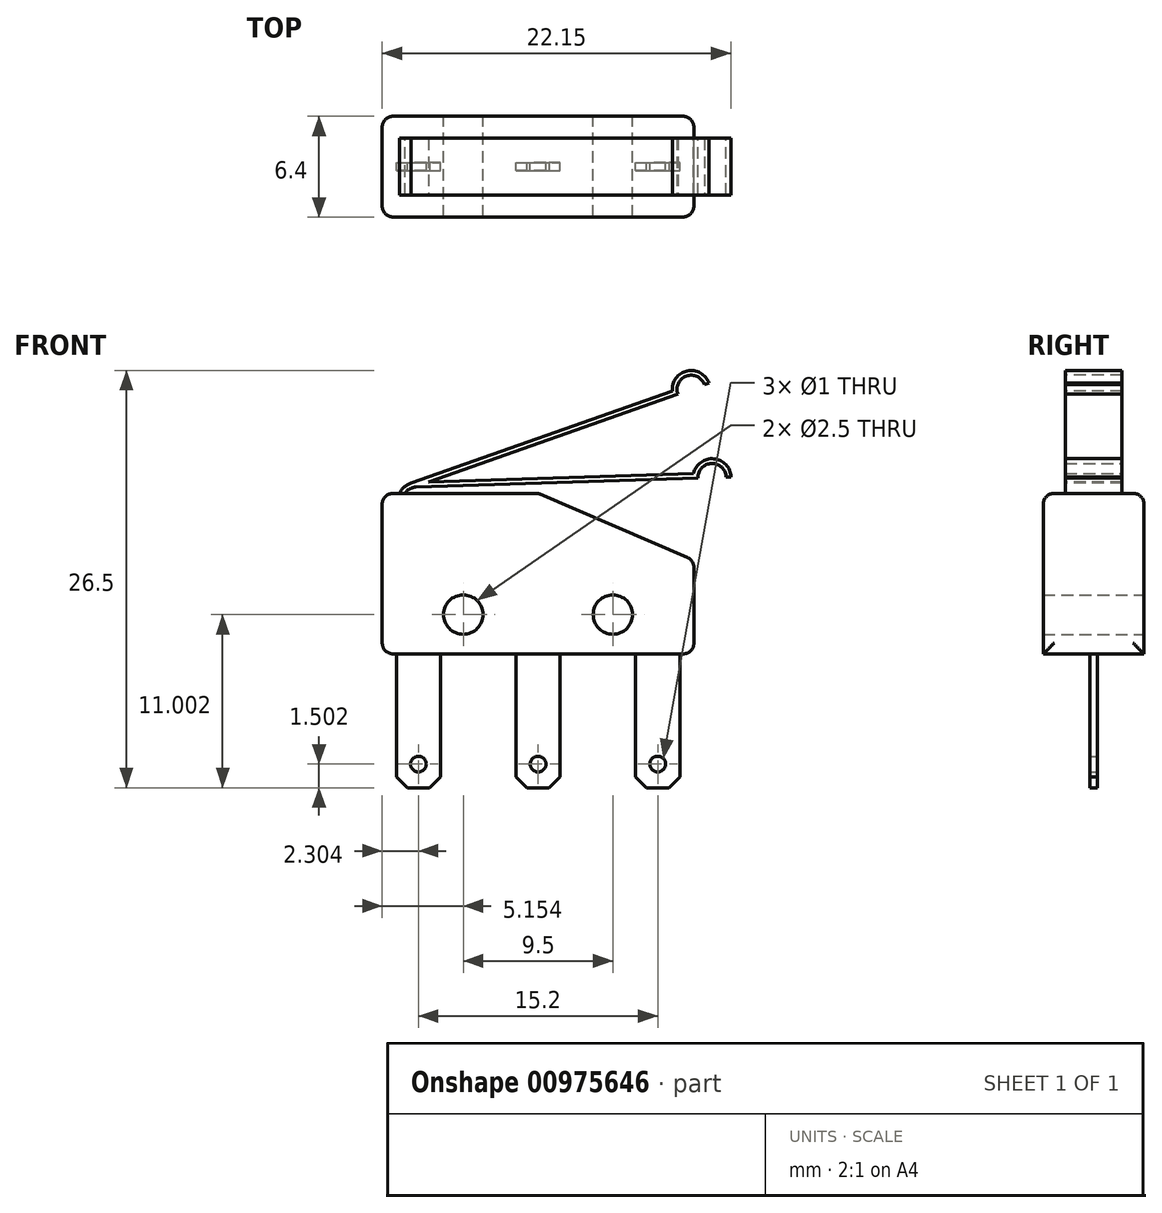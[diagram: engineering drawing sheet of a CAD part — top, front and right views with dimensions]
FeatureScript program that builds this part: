
annotation { "Feature Type Name" : "Feature", "Feature Type Description" : "" }
export const myFeature = defineFeature(function(context is Context, id is Id, definition is map)
    precondition{}
    {
        {
            var Q0;
            Q0=qCreatedBy(makeId("Front.planeOp"),FACE);
            var sketch = newSketch(context, id + "F0", { "sketchPlane" : qUnion([Q0])});
            skLineSegment(sketch, "E0.bottom", {"start": v(-24.17, 13.96) * mm, "end": v(-14.27, 13.96) * mm});
            skLineSegment(sketch, "E0.top", {"start": v(-24.17, 3.76) * mm, "end": v(-4.37, 3.76) * mm});
            skLineSegment(sketch, "E0.left", {"start": v(-24.17, 13.96) * mm, "end": v(-24.17, 3.76) * mm});
            skLineSegment(sketch, "E0.right", {"start": v(-4.37, 9.71) * mm, "end": v(-4.37, 3.76) * mm});
            skLineSegment(sketch, "E1", {"start": v(-24.17, 6.26) * mm, "end": v(-4.37, 6.26) * mm, "construction": true});
            skLineSegment(sketch, "E2", {"start": v(-14.27, 13.96) * mm, "end": v(-4.37, 9.71) * mm});
            skCircle(sketch, "E3", {"center": v(-19.02, 6.26) * mm, "radius": 1.25 * mm});
            skCircle(sketch, "E4", {"center": v(-9.52, 6.26) * mm, "radius": 1.25 * mm});
            skSolve(sketch);
        }
        {
            var Q0;
            Q0 = qSketchRegion(id + "F0", true);
            extrude(context, id + "F1", {"entities" : qUnion([Q0]), "endBound" : BoundingType.SYMMETRIC, "depth" : 6.4 * mm, "offsetDistance" : 25 * mm});
        }
        {
            var Q0;
            Q0=makeQuery(id+"F1.opExtrude","SWEPT_EDGE",EDGE,{"disambiguationData":[OSD([sQuery(id+"F0.wireOp",EDGE,"E0.right"),sQuery(id+"F0.wireOp",EDGE,"E2")])]});
            var Q1;
            Q1=makeQuery(id+"F1.opExtrude","SWEPT_EDGE",EDGE,{"disambiguationData":[OSD([sQuery(id+"F0.wireOp",EDGE,"E0.bottom"),sQuery(id+"F0.wireOp",EDGE,"E2")])]});
            var Q2;
            Q2=makeQuery(id+"F1.opExtrude","SWEPT_EDGE",EDGE,{"disambiguationData":[OSD([sQuery(id+"F0.wireOp",EDGE,"E0.bottom"),sQuery(id+"F0.wireOp",EDGE,"E0.left")])]});
            var Q3;
            Q3=makeQuery(id+"F1.opExtrude","SWEPT_EDGE",EDGE,{"disambiguationData":[OSD([sQuery(id+"F0.wireOp",EDGE,"E0.top"),sQuery(id+"F0.wireOp",EDGE,"E0.right")])]});
            var Q4;
            Q4=makeQuery(id+"F1.opExtrude","SWEPT_EDGE",EDGE,{"disambiguationData":[OSD([sQuery(id+"F0.wireOp",EDGE,"E0.top"),sQuery(id+"F0.wireOp",EDGE,"E0.left")])]});
            var Q5;
            Q5=makeQuery(id+"F1.opExtrude","CAP_EDGE",EDGE,{"disambiguationData":[OSD([sQuery(id+"F0.wireOp",EDGE,"E0.bottom")])],"isStart":false});
            var Q6;
            Q6=makeQuery(id+"F1.opExtrude","CAP_EDGE",EDGE,{"disambiguationData":[OSD([sQuery(id+"F0.wireOp",EDGE,"E2")])],"isStart":false});
            var Q7;
            Q7=makeQuery(id+"F1.opExtrude","CAP_EDGE",EDGE,{"disambiguationData":[OSD([sQuery(id+"F0.wireOp",EDGE,"E0.right")])],"isStart":false});
            var Q8;
            Q8=makeQuery(id+"F1.opExtrude","CAP_EDGE",EDGE,{"disambiguationData":[OSD([sQuery(id+"F0.wireOp",EDGE,"E0.right")])],"isStart":true});
            var Q9;
            Q9=makeQuery(id+"F1.opExtrude","CAP_EDGE",EDGE,{"disambiguationData":[OSD([sQuery(id+"F0.wireOp",EDGE,"E2")])],"isStart":true});
            var Q10;
            Q10=makeQuery(id+"F1.opExtrude","CAP_EDGE",EDGE,{"disambiguationData":[OSD([sQuery(id+"F0.wireOp",EDGE,"E0.bottom")])],"isStart":true});
            var Q11;
            Q11=makeQuery(id+"F1.opExtrude","CAP_EDGE",EDGE,{"disambiguationData":[OSD([sQuery(id+"F0.wireOp",EDGE,"E0.left")])],"isStart":false});
            var Q12;
            Q12=makeQuery(id+"F1.opExtrude","CAP_EDGE",EDGE,{"disambiguationData":[OSD([sQuery(id+"F0.wireOp",EDGE,"E0.left")])],"isStart":true});
            fillet(context, id + "F2", {"entities" : qUnion([Q0, Q1, Q2, Q3, Q4, Q5, Q6, Q7, Q8, Q9, Q10, Q11, Q12]), "tangentPropagation" : true, "radius" : 0.7 * mm, "defaultsChanged" : true, "vertexSettings" : [], "allowEdgeOverflow" : false});
        }
        {
            var Q0;
            Q0=qCreatedBy(makeId("Front.planeOp"),FACE);
            var sketch = newSketch(context, id + "F3", { "sketchPlane" : qUnion([Q0])});
            skLineSegment(sketch, "E5", {"start": v(-22.02, 14.66) * mm, "end": v(-4.39, 15.23) * mm});
            skLineSegment(sketch, "E6", {"start": v(-2.02, 15) * mm, "end": v(-2.32, 15) * mm});
            skLineSegment(sketch, "E7", {"start": v(-22, 14.36) * mm, "end": v(-22.02, 14.66) * mm, "construction": true});
            skArc(sketch, "E8", {"start": v(-2.32, 15) * mm, "mid": v(-3.24, 15.86) * mm, "end": v(-4.12, 14.93) * mm});
            skArc(sketch, "E9", {"start": v(-2.02, 15) * mm, "mid": v(-3.1, 16.16) * mm, "end": v(-4.39, 15.23) * mm});
            skLineSegment(sketch, "E10.trimOffspring", {"start": v(-4.12, 14.93) * mm, "end": v(-22, 14.36) * mm});
            skLineSegment(sketch, "E11", {"start": v(-23.44, 16.16) * mm, "end": v(-4.46, 16.16) * mm, "construction": true});
            skLineSegment(sketch, "E12", {"start": v(-19.02, 16.68) * mm, "end": v(-19.02, 5.07) * mm, "construction": true});
            skArc(sketch, "E13", {"start": v(-22.02, 14.66) * mm, "mid": v(-23.17, 13.57) * mm, "end": v(-22.22, 12.3) * mm});
            skArc(sketch, "E14", {"start": v(-22, 14.36) * mm, "mid": v(-22.86, 13.58) * mm, "end": v(-22.22, 12.61) * mm});
            skLineSegment(sketch, "E15", {"start": v(-22.22, 12.61) * mm, "end": v(-22.22, 12.3) * mm});
            skLineSegment(sketch, "E16", {"start": v(-23.32, 21.76) * mm, "end": v(-4.44, 21.76) * mm, "construction": true});
            skLineSegment(sketch, "E17", {"start": v(-3.22, 14.96) * mm, "end": v(-3.22, 23.39) * mm, "construction": true});
            skSolve(sketch);
        }
        {
            var Q0;
            Q0 = qSketchRegion(id + "F3", true);
            extrude(context, id + "F4", {"entities" : qUnion([Q0]), "operationType" : NewBodyOperationType.ADD, "endBound" : BoundingType.SYMMETRIC, "depth" : 3.6 * mm, "offsetDistance" : 25 * mm});
        }
        {
            var Q0;
            Q0=qCreatedBy(makeId("Front.planeOp"),FACE);
            var sketch = newSketch(context, id + "F5", { "sketchPlane" : qUnion([Q0])});
            skLineSegment(sketch, "E18.bottom", {"start": v(-23.27, 4.32) * mm, "end": v(-20.47, 4.32) * mm});
            skLineSegment(sketch, "E18.top", {"start": v(-23.27, -4.74) * mm, "end": v(-20.47, -4.74) * mm});
            skLineSegment(sketch, "E18.left", {"start": v(-23.27, 4.32) * mm, "end": v(-23.27, -4.74) * mm});
            skLineSegment(sketch, "E18.right", {"start": v(-20.47, 4.32) * mm, "end": v(-20.47, -4.74) * mm});
            skLineSegment(sketch, "E19.bottom", {"start": v(-15.67, 4.32) * mm, "end": v(-12.87, 4.32) * mm});
            skLineSegment(sketch, "E19.top", {"start": v(-15.67, -4.74) * mm, "end": v(-12.87, -4.74) * mm});
            skLineSegment(sketch, "E19.left", {"start": v(-15.67, 4.32) * mm, "end": v(-15.67, -4.74) * mm});
            skLineSegment(sketch, "E19.right", {"start": v(-12.87, 4.32) * mm, "end": v(-12.87, -4.74) * mm});
            skLineSegment(sketch, "E20.bottom", {"start": v(-8.07, 4.32) * mm, "end": v(-5.27, 4.32) * mm});
            skLineSegment(sketch, "E20.top", {"start": v(-8.07, -4.74) * mm, "end": v(-5.27, -4.74) * mm});
            skLineSegment(sketch, "E20.left", {"start": v(-8.07, 4.32) * mm, "end": v(-8.07, -4.74) * mm});
            skLineSegment(sketch, "E20.right", {"start": v(-5.27, 4.32) * mm, "end": v(-5.27, -4.74) * mm});
            skLineSegment(sketch, "E21", {"start": v(-21.87, -4.74) * mm, "end": v(-21.87, 4.32) * mm, "construction": true});
            skLineSegment(sketch, "E22", {"start": v(-21.87, 4.32) * mm, "end": v(-14.27, -4.74) * mm, "construction": true});
            skLineSegment(sketch, "E23", {"start": v(-14.27, -4.74) * mm, "end": v(-14.27, 4.32) * mm, "construction": true});
            skLineSegment(sketch, "E24", {"start": v(-14.27, 4.32) * mm, "end": v(-6.67, -4.74) * mm, "construction": true});
            skLineSegment(sketch, "E25", {"start": v(-6.67, -4.74) * mm, "end": v(-6.67, 4.32) * mm, "construction": true});
            skPoint(sketch, "E26", {"position": v(-14.27, 3.76) * mm});
            skLineSegment(sketch, "E27", {"start": v(-23.27, -3.24) * mm, "end": v(-5.27, -3.24) * mm, "construction": true});
            skCircle(sketch, "E28", {"center": v(-21.87, -3.24) * mm, "radius": 0.5 * mm});
            skCircle(sketch, "E29", {"center": v(-14.27, -3.24) * mm, "radius": 0.5 * mm});
            skCircle(sketch, "E30", {"center": v(-6.67, -3.24) * mm, "radius": 0.5 * mm});
            skSolve(sketch);
        }
        {
            var Q0;
            Q0 = qSketchRegion(id + "F5", true);
            extrude(context, id + "F6", {"entities" : qUnion([Q0]), "operationType" : NewBodyOperationType.ADD, "endBound" : BoundingType.SYMMETRIC, "depth" : 0.5 * mm, "offsetDistance" : 25 * mm});
        }
        {
            var Q0;
            Q0=makeQuery(id+"F6.opExtrude","SWEPT_EDGE",EDGE,{"disambiguationData":[OSD([sQuery(id+"F5.wireOp",EDGE,"E19.top"),sQuery(id+"F5.wireOp",EDGE,"E19.right")])]});
            var Q1;
            Q1=makeQuery(id+"F6.opExtrude","SWEPT_EDGE",EDGE,{"disambiguationData":[OSD([sQuery(id+"F5.wireOp",EDGE,"E19.top"),sQuery(id+"F5.wireOp",EDGE,"E19.left")])]});
            var Q2;
            Q2=makeQuery(id+"F6.opExtrude","SWEPT_EDGE",EDGE,{"disambiguationData":[OSD([sQuery(id+"F5.wireOp",EDGE,"E18.top"),sQuery(id+"F5.wireOp",EDGE,"E18.right")])]});
            var Q3;
            Q3=makeQuery(id+"F6.opExtrude","SWEPT_EDGE",EDGE,{"disambiguationData":[OSD([sQuery(id+"F5.wireOp",EDGE,"E18.top"),sQuery(id+"F5.wireOp",EDGE,"E18.left")])]});
            var Q4;
            Q4=makeQuery(id+"F6.opExtrude","SWEPT_EDGE",EDGE,{"disambiguationData":[OSD([sQuery(id+"F5.wireOp",EDGE,"E20.top"),sQuery(id+"F5.wireOp",EDGE,"E20.right")])]});
            var Q5;
            Q5=makeQuery(id+"F6.opExtrude","SWEPT_EDGE",EDGE,{"disambiguationData":[OSD([sQuery(id+"F5.wireOp",EDGE,"E20.top"),sQuery(id+"F5.wireOp",EDGE,"E20.left")])]});
            chamfer(context, id + "F7", {"entities" : qUnion([Q0, Q1, Q2, Q3, Q4, Q5]), "width" : 0.7 * mm, "tangentPropagation" : true});
        }
        {
            var Q0;
            Q0=makeQuery(id+"F4.opExtrude","CAP_FACE",FACE,{"disambiguationData":[OSD([sQuery(id+"F3.wireOp",EDGE,"E5"),sQuery(id+"F3.wireOp",EDGE,"E6"),sQuery(id+"F3.wireOp",EDGE,"E8"),sQuery(id+"F3.wireOp",EDGE,"E9"),sQuery(id+"F3.wireOp",EDGE,"E10.trimOffspring"),sQuery(id+"F3.wireOp",EDGE,"E13"),sQuery(id+"F3.wireOp",EDGE,"E14"),sQuery(id+"F3.wireOp",EDGE,"E15")])],"isStart":false});
            var sketch = newSketch(context, id + "F8", { "sketchPlane" : qUnion([Q0])});
            skLineSegment(sketch, "E31", {"start": v(-24.02, 21.76) * mm, "end": v(-1.58, 21.76) * mm, "construction": true});
            skLineSegment(sketch, "E32", {"start": v(-3.22, 14.96) * mm, "end": v(-3.22, 21.76) * mm, "construction": true});
            skArc(sketch, "E33", {"start": v(-3.41, 20.96) * mm, "mid": v(-4.8, 21.74) * mm, "end": v(-5.74, 20.46) * mm});
            skArc(sketch, "E34", {"start": v(-3.7, 20.86) * mm, "mid": v(-4.84, 21.41) * mm, "end": v(-5.4, 20.26) * mm});
            skArc(sketch, "E35", {"start": v(-22.27, 14.31) * mm, "mid": v(-22.86, 13.32) * mm, "end": v(-21.98, 12.58) * mm});
            skArc(sketch, "E36", {"start": v(-22.35, 14.6) * mm, "mid": v(-23.16, 13.28) * mm, "end": v(-21.98, 12.28) * mm});
            skLineSegment(sketch, "E37", {"start": v(-3.41, 20.96) * mm, "end": v(-3.7, 20.86) * mm});
            skLineSegment(sketch, "E38", {"start": v(-22.4, 14.59) * mm, "end": v(-5.74, 20.46) * mm});
            skLineSegment(sketch, "E39.trimOffspring", {"start": v(-5.4, 20.26) * mm, "end": v(-22.27, 14.31) * mm});
            skLineSegment(sketch, "E40", {"start": v(-21.98, 12.58) * mm, "end": v(-21.98, 12.28) * mm});
            skCircle(sketch, "E41", {"center": v(-21.98, 13.47) * mm, "radius": 18.82 * mm, "construction": true});
            skSolve(sketch);
        }
        {
            var Q0;
            Q0 = qSketchRegion(id + "F8", true);
            var Q1;
            Q1=makeQuery(id+"F4.opExtrude","CAP_FACE",FACE,{"disambiguationData":[OSD([sQuery(id+"F3.wireOp",EDGE,"E5"),sQuery(id+"F3.wireOp",EDGE,"E6"),sQuery(id+"F3.wireOp",EDGE,"E8"),sQuery(id+"F3.wireOp",EDGE,"E9"),sQuery(id+"F3.wireOp",EDGE,"E10.trimOffspring"),sQuery(id+"F3.wireOp",EDGE,"E13"),sQuery(id+"F3.wireOp",EDGE,"E14"),sQuery(id+"F3.wireOp",EDGE,"E15")])],"isStart":true});
            extrude(context, id + "F9", {"entities" : qUnion([Q0]), "operationType" : NewBodyOperationType.ADD, "endBound" : BoundingType.UP_TO_SURFACE, "oppositeDirection" : true, "depth" : 25 * mm, "endBoundEntityFace" : qUnion([Q1]), "offsetDistance" : 25 * mm});
        }
    });
